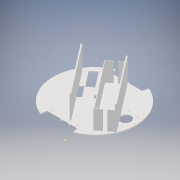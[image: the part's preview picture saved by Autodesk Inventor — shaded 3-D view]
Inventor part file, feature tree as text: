
AUTODESK INVENTOR PART (.ipt)
format: ipt  version: 2020 (Build 240168000, 168)  size: 327,680 bytes
history: native  units: mm
features: sketch x10, extrude x9, reference x9, other x3, projected_geometry x1
ambient origin geometry x8: Origin, YZ Plane, XZ Plane, XY Plane, X Axis, Y Axis, Z Axis, Center Point
bodies: Solid1 (feature_tree)
feature tree (32):
  extrude  "DnoKonstrukcije"  Depth=34.0mm TaperAngle=0.0deg
  extrude  "DrzacZaBateriju"  Depth=42.0mm TaperAngle=0.0deg
  extrude  "DrzacZaTeensy"  Depth=30.0mm
  extrude  "DrzacZaPDB"  Depth=35.0mm
  sketch  "Sketch10"  dims[d19=2.0mm d20=2.0mm]
  extrude  "RupeZaPDBSEkranom"  Depth=2.0mm
  extrude  "RupeZaDriverMotora"  Depth=2.0mm
  extrude  "RupeZaPDB"  Depth=30.0mm
  extrude  "RupeZaTeensy"  Depth=35.0mm
  extrude  "RupaZaLezaj"  Depth=2.0mm
  sketch  "Sketch1"  dims[d0=2.0mm d1=0.0mm d8=34.0mm d9=0.0mm]
  reference  "Reference7"
  sketch  "Sketch6"  dims[d10=10.0mm d11=0.0mm d12=42.0mm d13=0.0mm]
  reference  "Reference10"
  reference  "Reference11"
  reference  "Reference12"
  reference  "Reference13"
  sketch  "Sketch7"  dims[d14=2.0mm d15=0.0mm d16=30.0mm]
  projected_geometry  "Projected Loop2"
  sketch  "Sketch8"  dims[d17=35.0mm d18=2.5mm]
  reference  "Reference14"
  sketch  "Sketch11"  dims[d21=2.0mm d22=2.0mm]
  reference  "Reference17"
  reference  "Reference18"
  reference  "Reference19"
  sketch  "Sketch12"  dims[d23=2.0mm d24=0.0mm d25=30.0mm]
  sketch  "Sketch15"  dims[d26=35.0mm d27=2.5mm]
  sketch  "Sketch16"  dims[d28=2.0mm d29=2.0mm]
  sketch  "Sketch17"  dims[d30=2.0mm d31=2.0mm d32=2.0mm d33=0.0mm d34=65.0mm d35=35.0mm d36=2.5mm d37=2.0mm d38=2.0mm d39=2.0mm d40=2.0mm d41=2.0mm d42=0.0mm d43=58.784mm d44=19.0mm d45=2.0mm d46=0.0mm]
  other  "DonjaKons_V.5 - Copy.iam"
  other  "KonstrukcijaDonjiDio_v.3.:1"
  other  "mrm-ps3xc:1"
